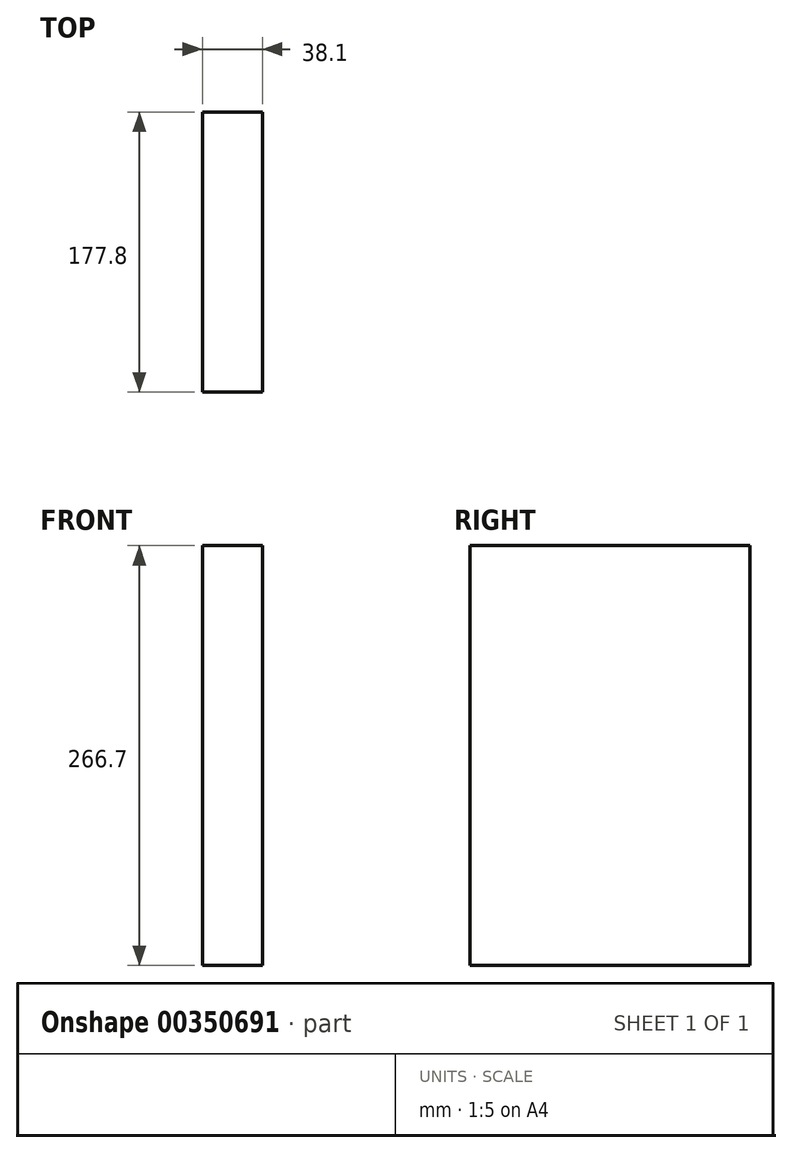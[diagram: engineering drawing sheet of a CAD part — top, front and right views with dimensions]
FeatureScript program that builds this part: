
annotation { "Feature Type Name" : "Feature", "Feature Type Description" : "" }
export const myFeature = defineFeature(function(context is Context, id is Id, definition is map)
    precondition{}
    {
        {
            var Q0;
            Q0=qCreatedBy(makeId("Front.planeOp"),FACE);
            var sketch = newSketch(context, id + "F0", { "sketchPlane" : qUnion([Q0])});
            skLineSegment(sketch, "E0.bottom", {"start": v(19.05, 133.35) * mm, "end": v(-19.05, 133.35) * mm});
            skLineSegment(sketch, "E0.top", {"start": v(19.05, -133.35) * mm, "end": v(-19.05, -133.35) * mm});
            skLineSegment(sketch, "E0.left", {"start": v(19.05, 133.35) * mm, "end": v(19.05, -133.35) * mm});
            skLineSegment(sketch, "E0.right", {"start": v(-19.05, 133.35) * mm, "end": v(-19.05, -133.35) * mm});
            skPoint(sketch, "E0.middle", {"position": v(0, 0) * mm});
            skSolve(sketch);
        }
        {
            var Q0;
            Q0=makeQuery(id+"F0.imprint","IMPRINT",FACE,{"disambiguationData":[TD([[makeQuery(id+"F0.imprint","IMPRINT",EDGE,{"derivedFrom":sQuery(id+"F0.wireOp",EDGE,"E0.bottom")}),1.0]])]});
            extrude(context, id + "F1", {"entities" : qUnion([Q0]), "oppositeDirection" : true, "depth" : 177.8 * mm});
        }
    });
